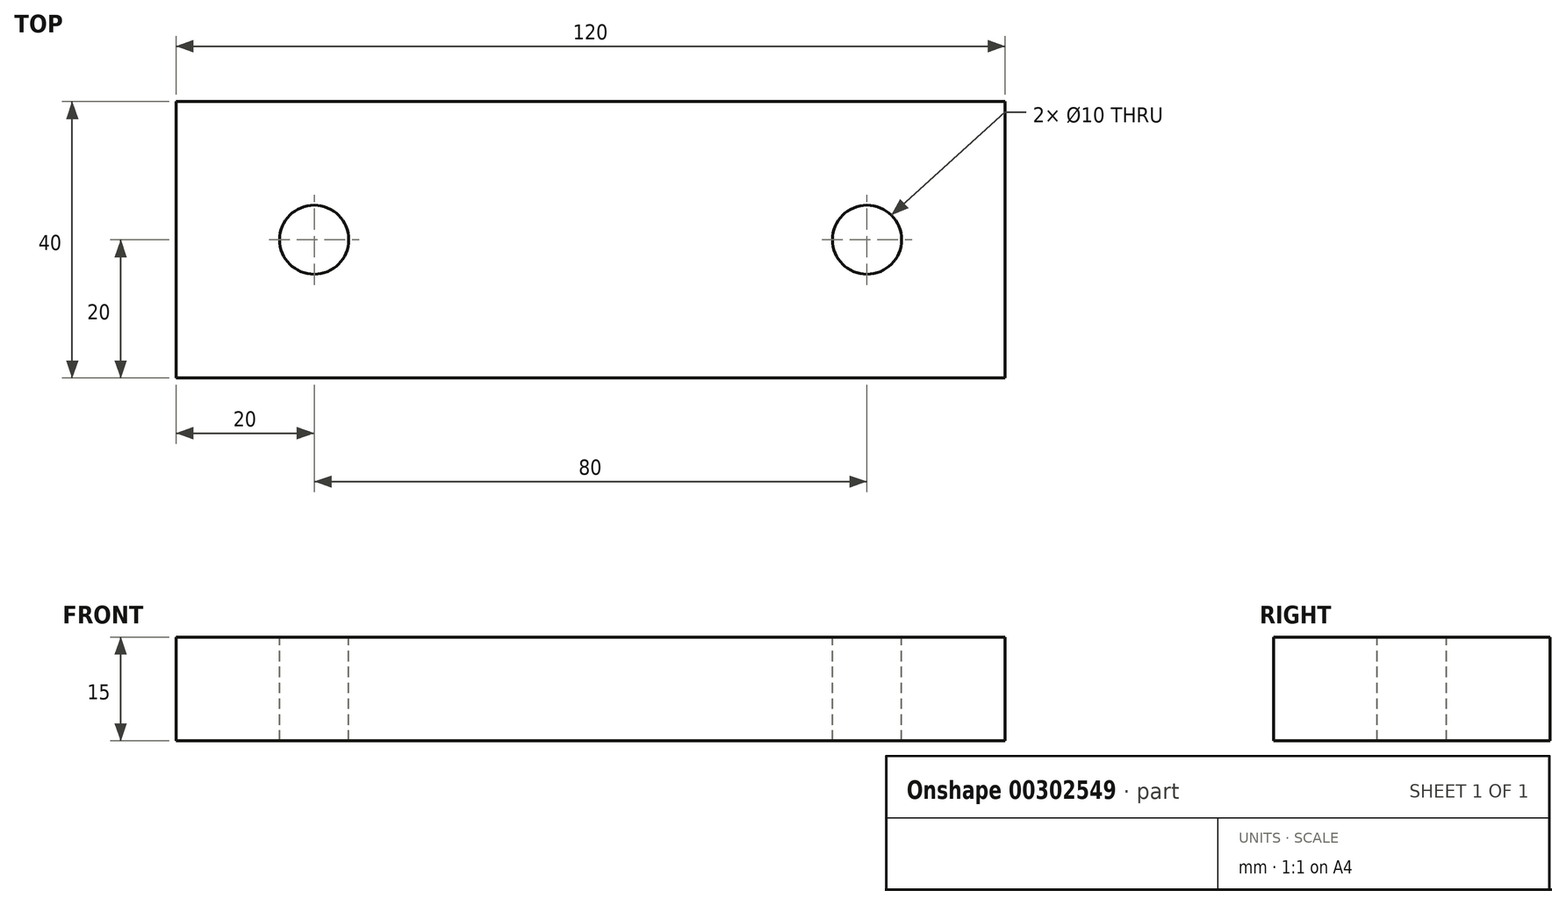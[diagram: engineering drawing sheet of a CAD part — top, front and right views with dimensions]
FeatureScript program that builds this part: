
annotation { "Feature Type Name" : "Feature", "Feature Type Description" : "" }
export const myFeature = defineFeature(function(context is Context, id is Id, definition is map)
    precondition{}
    {
        {
            var Q0;
            Q0=qCreatedBy(makeId("Top.planeOp"),FACE);
            var sketch = newSketch(context, id + "F0", { "sketchPlane" : qUnion([Q0])});
            skLineSegment(sketch, "E0.bottom", {"start": v(0, 0) * mm, "end": v(120, 0) * mm});
            skLineSegment(sketch, "E0.top", {"start": v(0, 40) * mm, "end": v(120, 40) * mm});
            skLineSegment(sketch, "E0.left", {"start": v(0, 0) * mm, "end": v(0, 40) * mm});
            skLineSegment(sketch, "E0.right", {"start": v(120, 0) * mm, "end": v(120, 40) * mm});
            skCircle(sketch, "E1", {"center": v(20, 20) * mm, "radius": 5 * mm});
            skCircle(sketch, "E2", {"center": v(100, 20) * mm, "radius": 5 * mm});
            skSolve(sketch);
        }
        {
            var Q0;
            Q0 = qSketchRegion(id + "F0", true);
            extrude(context, id + "F1", {"entities" : qUnion([Q0]), "oppositeDirection" : true, "depth" : 15 * mm});
        }
    });
